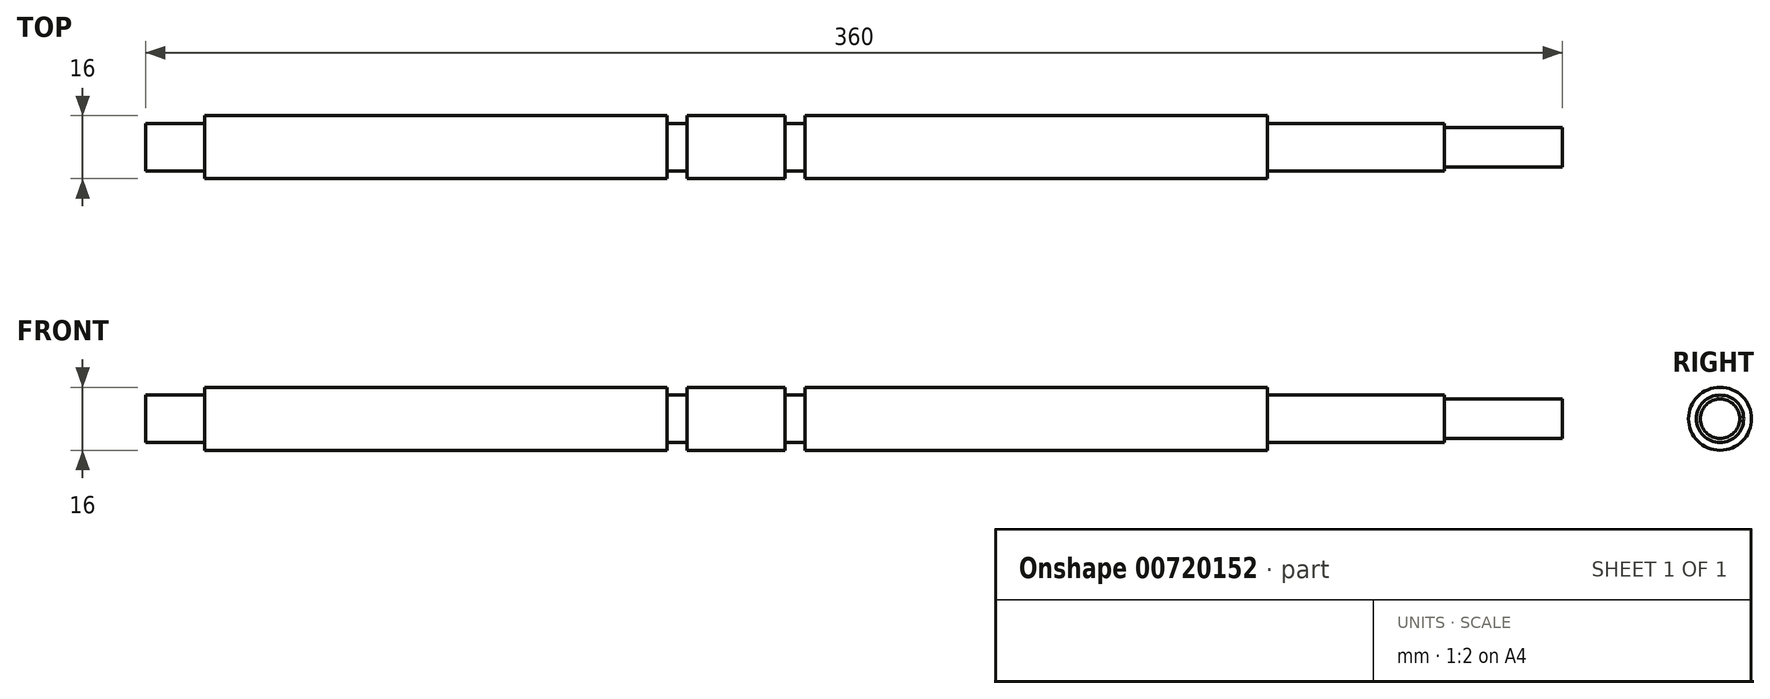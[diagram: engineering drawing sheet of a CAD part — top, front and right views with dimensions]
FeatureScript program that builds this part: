
annotation { "Feature Type Name" : "Feature", "Feature Type Description" : "" }
export const myFeature = defineFeature(function(context is Context, id is Id, definition is map)
    precondition{}
    {
        {
            var Q0;
            Q0=qCreatedBy(makeId("Front.planeOp"),FACE);
            var sketch = newSketch(context, id + "F0", { "sketchPlane" : qUnion([Q0])});
            skLineSegment(sketch, "E0", {"start": v(0, 0) * mm, "end": v(360, 0) * mm});
            skLineSegment(sketch, "E1", {"start": v(360, 0) * mm, "end": v(360, 5) * mm});
            skLineSegment(sketch, "E2", {"start": v(360, 5) * mm, "end": v(330, 5) * mm});
            skLineSegment(sketch, "E3", {"start": v(330, 5) * mm, "end": v(330, 6) * mm});
            skLineSegment(sketch, "E4", {"start": v(330, 6) * mm, "end": v(285, 6) * mm});
            skLineSegment(sketch, "E5", {"start": v(285, 6) * mm, "end": v(285, 8) * mm});
            skLineSegment(sketch, "E6", {"start": v(285, 8) * mm, "end": v(167.5, 8) * mm});
            skLineSegment(sketch, "E7.0", {"start": v(15, 8) * mm, "end": v(15, 6) * mm});
            skLineSegment(sketch, "E8", {"start": v(0, 0) * mm, "end": v(0, 6) * mm});
            skLineSegment(sketch, "E9", {"start": v(0, 6) * mm, "end": v(15, 6) * mm});
            skLineSegment(sketch, "E10.0", {"start": v(132.5, 8) * mm, "end": v(132.5, 6) * mm});
            skLineSegment(sketch, "E11", {"start": v(132.5, 6) * mm, "end": v(137.5, 6) * mm});
            skLineSegment(sketch, "E12", {"start": v(137.5, 6) * mm, "end": v(137.5, 8) * mm});
            skLineSegment(sketch, "E13.trimOffspring", {"start": v(132.5, 8) * mm, "end": v(15, 8) * mm});
            skLineSegment(sketch, "E14.0", {"start": v(162.5, 6) * mm, "end": v(162.5, 8) * mm});
            skLineSegment(sketch, "E15", {"start": v(162.5, 6) * mm, "end": v(167.5, 6) * mm});
            skLineSegment(sketch, "E16", {"start": v(167.5, 6) * mm, "end": v(167.5, 8) * mm});
            skLineSegment(sketch, "E17.trimOffspring", {"start": v(162.5, 8) * mm, "end": v(137.5, 8) * mm});
            skSolve(sketch);
        }
        {
            var Q0;
            Q0=makeQuery(id+"F0.imprint","IMPRINT",FACE,{"disambiguationData":[TD([[makeQuery(id+"F0.imprint","IMPRINT",EDGE,{"derivedFrom":sQuery(id+"F0.wireOp",EDGE,"E0")}),1.0]])]});
            var Q1;
            Q1=sQuery(id+"F0.wireOp",EDGE,"E0");
            revolve(context, id + "F1", {"surfaceOperationType" : NewSurfaceOperationType.NEW, "entities" : qUnion([Q0]), "axis" : qUnion([Q1]), "revolveType" : RevolveType.FULL});
        }
    });
